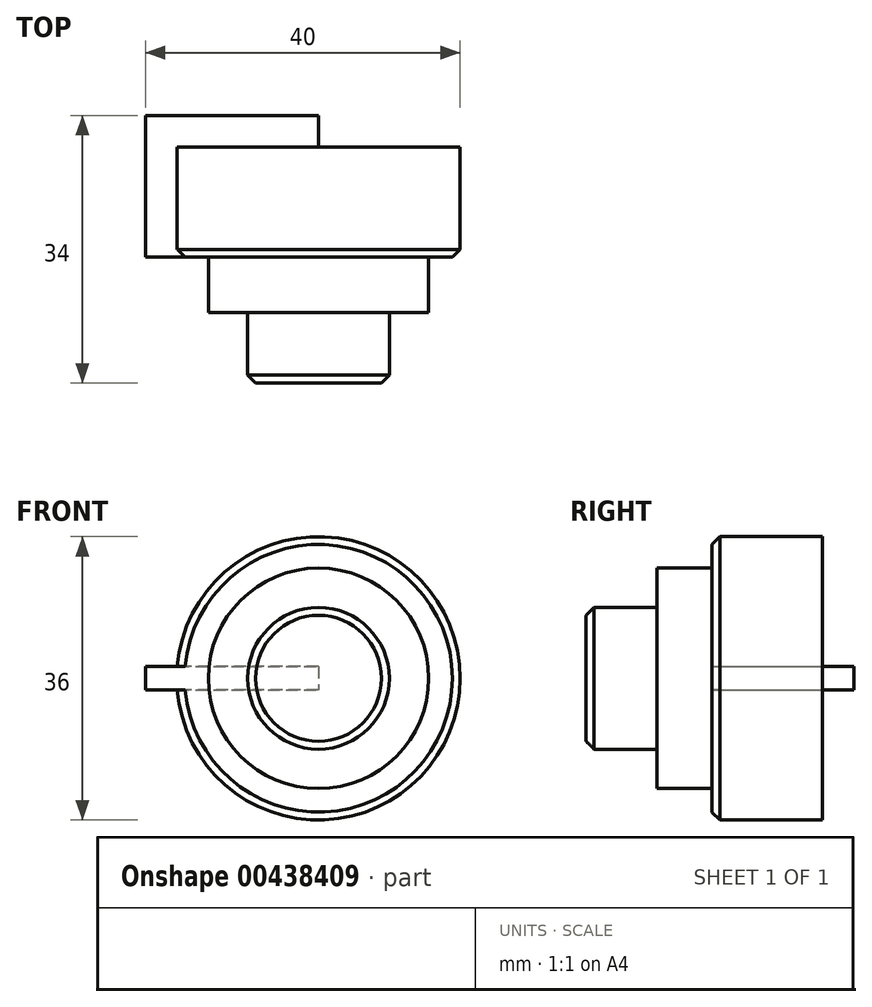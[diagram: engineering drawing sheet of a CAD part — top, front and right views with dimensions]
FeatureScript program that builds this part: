
annotation { "Feature Type Name" : "Feature", "Feature Type Description" : "" }
export const myFeature = defineFeature(function(context is Context, id is Id, definition is map)
    precondition{}
    {
        {
            var Q0;
            Q0=qCreatedBy(makeId("Front.planeOp"),FACE);
            var sketch = newSketch(context, id + "F0", { "sketchPlane" : qUnion([Q0])});
            skCircle(sketch, "E0", {"center": v(0, 0) * mm, "radius": 18 * mm});
            skSolve(sketch);
        }
        {
            var Q0;
            Q0 = qSketchRegion(id + "F0", true);
            extrude(context, id + "F1", {"entities" : qUnion([Q0]), "endBound" : BoundingType.SYMMETRIC, "depth" : 14 * mm});
        }
        {
            var Q0;
            Q0=qCreatedBy(makeId("Front.planeOp"),FACE);
            var sketch = newSketch(context, id + "F2", { "sketchPlane" : qUnion([Q0])});
            skCircle(sketch, "E1", {"center": v(0, 0) * mm, "radius": 14 * mm});
            skSolve(sketch);
        }
        {
            var Q0;
            Q0 = qSketchRegion(id + "F2", true);
            extrude(context, id + "F3", {"entities" : qUnion([Q0]), "operationType" : NewBodyOperationType.ADD, "depth" : 14 * mm});
        }
        {
            var Q0;
            Q0=qCreatedBy(makeId("Front.planeOp"),FACE);
            var sketch = newSketch(context, id + "F4", { "sketchPlane" : qUnion([Q0])});
            skCircle(sketch, "E2", {"center": v(0, 0) * mm, "radius": 9 * mm});
            skSolve(sketch);
        }
        {
            var Q0;
            Q0 = qSketchRegion(id + "F4", true);
            extrude(context, id + "F5", {"entities" : qUnion([Q0]), "operationType" : NewBodyOperationType.ADD, "depth" : 23 * mm});
        }
        {
            var Q0;
            Q0=qCreatedBy(makeId("Front.planeOp"),FACE);
            var sketch = newSketch(context, id + "F6", { "sketchPlane" : qUnion([Q0])});
            skLineSegment(sketch, "E3.bottom", {"start": v(0, -1.5) * mm, "end": v(-22, -1.5) * mm});
            skLineSegment(sketch, "E3.top", {"start": v(0, 1.5) * mm, "end": v(-22, 1.5) * mm});
            skLineSegment(sketch, "E3.left", {"start": v(0, -1.5) * mm, "end": v(0, 1.5) * mm});
            skLineSegment(sketch, "E3.right", {"start": v(-22, -1.5) * mm, "end": v(-22, 1.5) * mm});
            skPoint(sketch, "E3.middle", {"position": v(-11, 0) * mm});
            skSolve(sketch);
        }
        {
            var Q0;
            Q0 = qSketchRegion(id + "F6", true);
            extrude(context, id + "F7", {"entities" : qUnion([Q0]), "operationType" : NewBodyOperationType.ADD, "depth" : 7 * mm, "hasSecondDirection" : true, "secondDirectionOppositeDirection" : true, "secondDirectionDepth" : 11 * mm});
        }
        {
            var Q0;
            Q0=makeQuery(id+"F5.opExtrude","CAP_EDGE",EDGE,{"disambiguationData":[OSD([sQuery(id+"F4.wireOp",EDGE,"E2")])],"isStart":false});
            chamfer(context, id + "F8", {"entities" : qUnion([Q0]), "width" : 1 * mm});
        }
        {
            var Q0;
            Q0=makeQuery(id+"F1.opExtrude","CAP_EDGE",EDGE,{"disambiguationData":[OSD([sQuery(id+"F0.wireOp",EDGE,"E0")])],"isStart":false});
            chamfer(context, id + "F9", {"entities" : qUnion([Q0]), "width" : 1 * mm, "tangentPropagation" : true});
        }
    });
